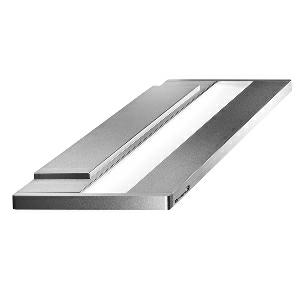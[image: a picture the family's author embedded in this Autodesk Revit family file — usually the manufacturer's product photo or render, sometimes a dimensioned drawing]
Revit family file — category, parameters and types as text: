
# Revit family: zera_bed_-_zew_7000_830_00813014_a49b
name_source: partatom
category: Lighting Fixtures
units: mm (PartAtom-declared; Revit-internal decimal feet)

## family parameters
Cut with Voids When Loaded = No
Host = Face
Light Source = No
Part Type = Normal
Room Calculation Point = No
Round Connector Dimension = Use Diameter
Shared = No

## types (1)
- AL+LL (1 x LED, 6900 lm, 4000K/3000K)
    Apparent Load = 61 VA
    Approval mark = CE
    CIE Flux Codes = 49 80 96 25 100
    Color Rendering = 90/80
    Color Temperature = 4000K/3000K
    Default Elevation = 2000 mm  [stored 6.56168 ft]
    Description = ZEW 7000/830|Wall-mounted luminaire|light source:   Warm white   |work equipment: Power supply unit|luminous flux: 6900 lm|light distribution: Direct/indirect|class of protection: I|technology: Switchable|mains lead: Connector 5 pin|glare control: Diffusor|special features: General light, indirect, 3000K, Ra80, DIN EN 60598-2-25, Reading light, direct, 3,00K, Ra80|
    Frequency = 50 Hz, 60 Hz
    Height = 20 mm  [stored 0.0656168 ft]
    Lamp = 1 x LED
    Lamp Light Flux = 6900 lm
    Lamp count = 1
    Length = 1050 mm
    Luminous efficacy = 113 lm/W
    Manufacturer = Waldmann
    ModVariant = No
    Model = 00813014
    Mounting Place = Wall
    Mounting Type = Surface mounted
    Number of Poles = 1
    OnlyDefault = Yes
    Power Factor = 1
    Product Name = ZERA.bed - ZEW 7000/830
    Product group = Wall mounted Luminaire
    ProductGroupID = 20
    Protection Class = Protection class I
    Protection Degree = IP 20
    RLX_Detail_Level = 1
    RLX_Emergency_Light_Flux = 0 lm
    RLX_Emergency_Type = 0
    RLX_Emergency_Type_DB = No
    RlxData = <blob elided: 69745 chars, md5=69d76eb3>
    Socket = socket
    Standby Power = 0 W
    System Light Flux = 6900 lm
    System Power = 61 W
    Type Comments = Allgemeinlicht und Leselicht
    Type Image = zera_bed.jpg
    URL = http://relux.com
    VarID = al_ll_67c3
    Voltage = 230 V
    Voltage Range = 220-240 V
    Weight = 0.00 kg
    Width = 230 mm

note: [stored X ft] marks values corroborated as IEEE doubles in the binary element streams (Revit-internal decimal feet)

## geometry (parser evidence)
native form markers: Blend x4, Sweep x15
no freeform markers — native parametric forms only
